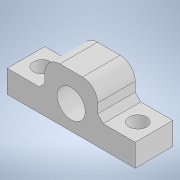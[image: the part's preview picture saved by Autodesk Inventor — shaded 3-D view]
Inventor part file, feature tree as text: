
AUTODESK INVENTOR PART (.ipt)
format: ipt  version: 2021 (Build 250183000, 183)  size: 145,920 bytes
history: native  units: mm
features: extrude x4, sketch x4, fillet x1, chamfer x1
ambient origin geometry x8: Origin, YZ Plane, XZ Plane, XY Plane, X Axis, Y Axis, Z Axis, Center Point
bodies: Solid1 (feature_tree)
feature tree (10):
  extrude  "Extrusion1"  Depth=10.0mm
  extrude  "Extrusion2"  Depth=6.0mm
  extrude  "Extrusion3"  Depth=4.65mm
  extrude  "Extrusion4"  Depth=10.0mm
  fillet  "Fillet2"  Radius=4.3mm
  chamfer  "Chamfer1"  [1 undecoded]
  sketch  "Sketch1"  dims[d0=34.0mm d1=10.0mm]
  sketch  "Sketch3"  dims[d2=6.0mm d3=0.0mm d4=4.65mm]
  sketch  "Sketch4"  dims[d5=5.0mm d6=4.65mm]
  sketch  "Sketch6"  dims[d7=5.0mm d9=4.3mm d10=4.3mm d11=0.0mm d12=0.0mm d16=8.0mm d17=0.0mm d26=7.45mm d29=0.0mm d30=0.0mm d31=4.0mm d34=14.0mm d35=10.0mm d36=7.62mm d37=7.0mm d39=1.5mm d40=2.0mm d41=45.0deg]
note: 1 required parameter value undecoded (feature->parameter linkage not recoverable at this tier; creation-order binding heuristic only, values carry confidence <= 0.55)
